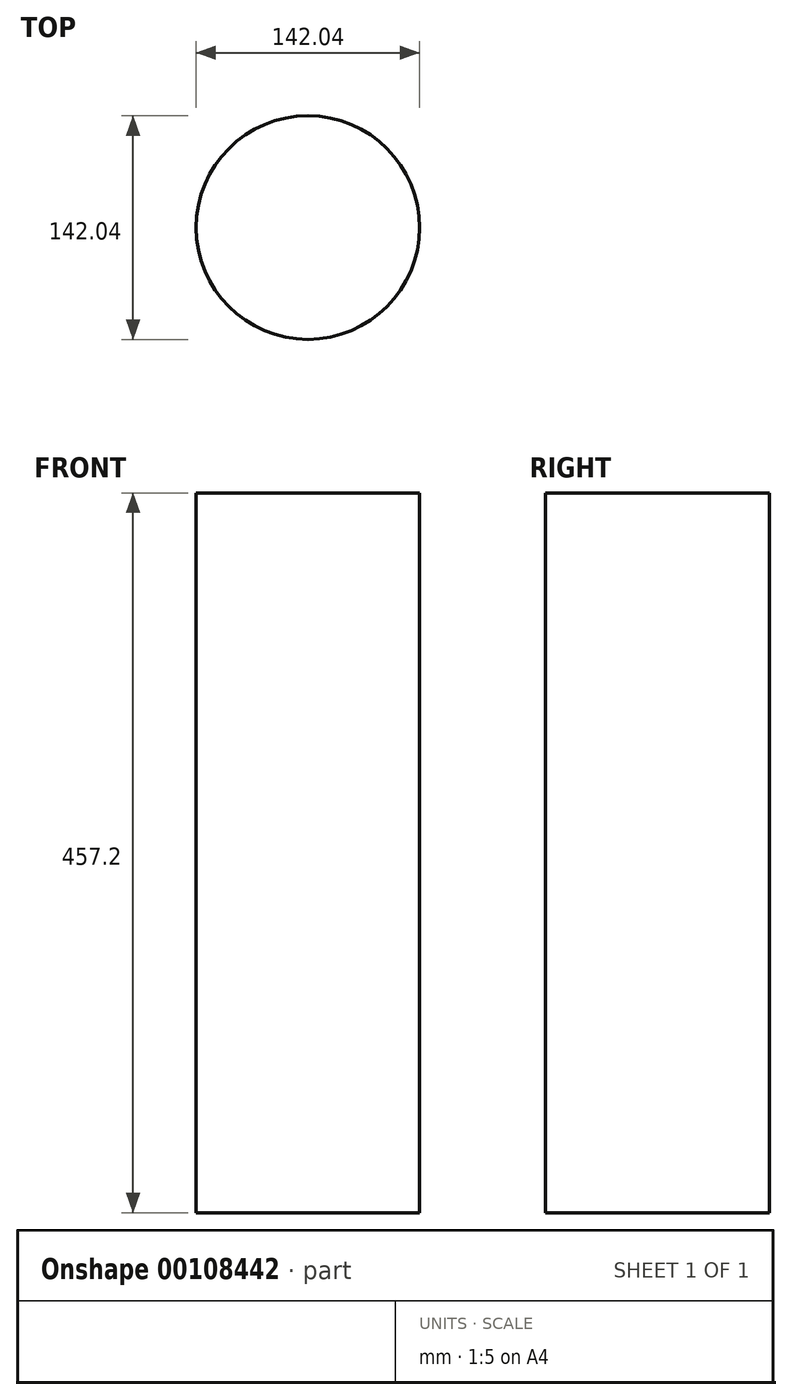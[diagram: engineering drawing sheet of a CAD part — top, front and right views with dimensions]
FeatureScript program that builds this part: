
annotation { "Feature Type Name" : "Feature", "Feature Type Description" : "" }
export const myFeature = defineFeature(function(context is Context, id is Id, definition is map)
    precondition{}
    {
        {
            var Q0;
            Q0=qCreatedBy(makeId("Top.planeOp"),FACE);
            var sketch = newSketch(context, id + "F0", { "sketchPlane" : qUnion([Q0])});
            skCircle(sketch, "E0", {"center": v(0, 0) * mm, "radius": 71.02 * mm});
            skSolve(sketch);
        }
        {
            var Q0;
            Q0=makeQuery(id+"F0.imprint","IMPRINT",FACE,{"disambiguationData":[TD([[makeQuery(id+"F0.imprint","IMPRINT",EDGE,{"derivedFrom":sQuery(id+"F0.wireOp",EDGE,"E0")}),1.0]])]});
            extrude(context, id + "F1", {"entities" : qUnion([Q0]), "depth" : 457.2 * mm});
        }
    });
